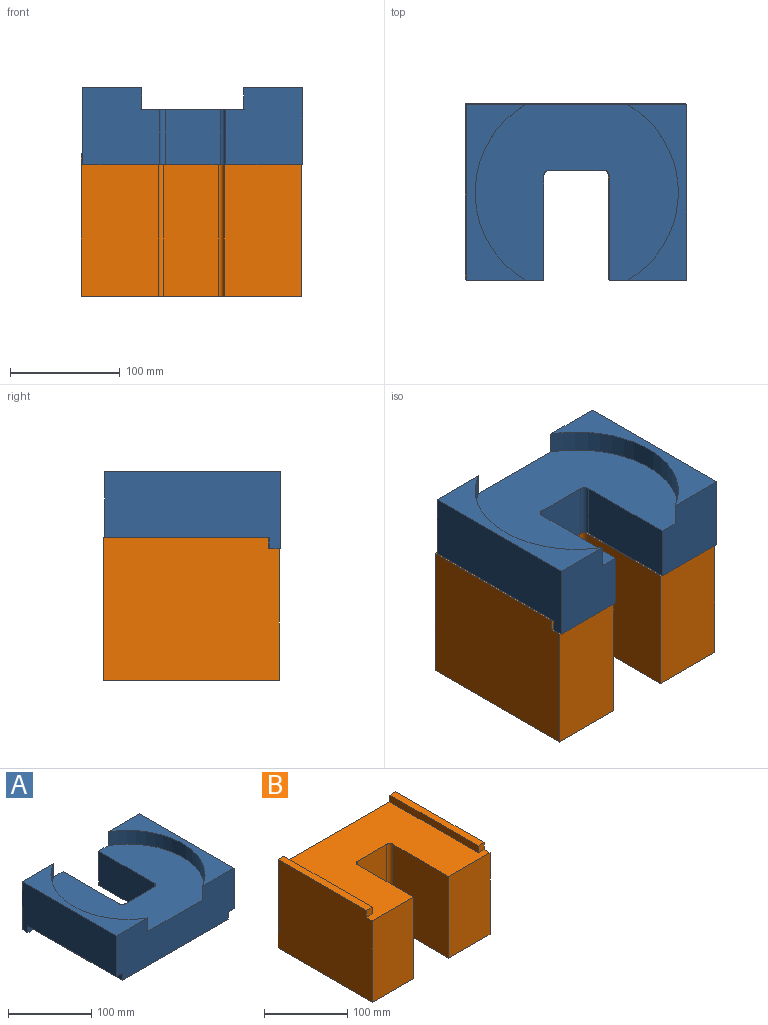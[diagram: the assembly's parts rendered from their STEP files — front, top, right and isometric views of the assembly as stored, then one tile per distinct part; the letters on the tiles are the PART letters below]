
ASSEMBLY  parts=2 mates=1
PART A: 22 faces, bbox 200x160x70 mm
  f0: plane 200x70mm, normal (0,-1,0), area 11942.6mm2, adj f1,f2,f4,f5,f7,f8,f9,f10
  f1: plane 160x70mm, normal (-1,0,0), area 9700mm2, adj f0,f4,f6,f8,f14,f16
  f2: plane 185x160mm, normal (0,0,1), area 19320.9mm2, adj f0,f3,f6,f7,f9,f11,f12,f13
  f3: plane 70x70mm, normal (0,1,0), area 4571.3mm2, adj f2,f4,f5,f9,f10,f12
  f4: plane 200x160mm, normal (0,0,-1), area 23010.7mm2, adj f0,f1,f3,f5,f6,f11,f12,f13
  f5: plane 160x70mm, normal (1,0,0), area 9700mm2, adj f0,f3,f4,f10,f17,f19
  f6: plane 70x70mm, normal (0,1,0), area 4571.3mm2, adj f1,f2,f4,f7,f8,f13
  f7: cylinder r=92.5mm len=160mm, axis (0,0,-1), area 3866.1mm2, adj f0,f2,f6,f8
  f8: plane 160x53.56mm, normal (0,0,1), area 3344.9mm2, adj f0,f1,f6,f7
  f9: cylinder r=92.5mm len=160mm, axis (0,0,-1), area 3866.1mm2, adj f0,f2,f3,f10
  f10: plane 160x53.56mm, normal (0,0,1), area 3344.9mm2, adj f0,f3,f5,f9
  f11: plane 50x50mm, normal (0,1,0), area 2500mm2, adj f2,f4,f20,f21
  f12: plane 95x50mm, normal (-1,0,0), area 4750mm2, adj f2,f3,f4,f21
  f13: plane 95x50mm, normal (1,0,0), area 4750mm2, adj f2,f4,f6,f20
  f14: plane 150x10mm, normal (0,0,-1), area 1500mm2, adj f0,f1,f15,f16
  f15: plane 150x10mm, normal (-1,0,0), area 1500mm2, adj f0,f4,f14,f16
  f16: plane 10x10mm, normal (0,-1,0), area 100mm2, adj f1,f4,f14,f15
  f17: plane 150x10mm, normal (0,0,-1), area 1500mm2, adj f0,f5,f18,f19
  f18: plane 150x10mm, normal (1,0,0), area 1500mm2, adj f0,f4,f17,f19
  f19: plane 10x10mm, normal (0,-1,0), area 100mm2, adj f4,f5,f17,f18
  f20: cylinder r=5mm len=50mm, axis (0,0,1), area 392.7mm2, adj f2,f4,f11,f13
  f21: cylinder r=5mm len=50mm, axis (0,0,-1), area 392.7mm2, adj f2,f4,f11,f12
PART B: 26 faces, bbox 200x160x130 mm
  f0: plane 200x160mm, normal (0,0,1), area 23010.7mm2, adj f1,f2,f3,f4,f5,f6,f7,f8
  f1: plane 120x95mm, normal (-1,0,0), area 11400mm2, adj f0,f2,f9,f25
  f2: plane 120x70mm, normal (0,-1,0), area 8400mm2, adj f0,f1,f3,f9
  f3: plane 160x130mm, normal (1,0,0), area 20700mm2, adj f0,f2,f4,f9,f11,f12
  f4: plane 200x130mm, normal (0,1,0), area 24200mm2, adj f0,f3,f5,f9,f10,f11,f13,f14
  f5: plane 160x130mm, normal (-1,0,0), area 20700mm2, adj f0,f4,f6,f9,f13,f15
  f6: plane 120x70mm, normal (0,-1,0), area 8400mm2, adj f0,f5,f7,f9
  f7: plane 120x95mm, normal (1,0,0), area 11400mm2, adj f0,f6,f9,f24
  f8: plane 120x50mm, normal (0,-1,0), area 6000mm2, adj f0,f9,f24,f25
  f9: plane 200x160mm, normal (0,0,-1), area 25756.3mm2, adj f1,f2,f3,f4,f5,f6,f7,f8
  f10: plane 150x10mm, normal (-1,0,0), area 1500mm2, adj f0,f4,f11,f12
  f11: plane 150x10mm, normal (0,0,1), area 1500mm2, adj f3,f4,f10,f12
  f12: plane 10x10mm, normal (0,-1,0), area 100mm2, adj f0,f3,f10,f11
  f13: plane 150x10mm, normal (0,0,1), area 1500mm2, adj f4,f5,f14,f15
  f14: plane 150x10mm, normal (1,0,0), area 1500mm2, adj f0,f4,f13,f15
  f15: plane 10x10mm, normal (0,-1,0), area 100mm2, adj f0,f5,f13,f14
  f16: cone r=0mm half-angle=59deg, axis (0,0,-1), area 74.2mm2, adj f17
  f17: cylinder r=4.5mm len=15mm, axis (0,0,-1), area 424.1mm2, adj f9,f16
  f18: cone r=0mm half-angle=59deg, axis (0,0,-1), area 74.2mm2, adj f19
  f19: cylinder r=4.5mm len=15mm, axis (0,0,-1), area 424.1mm2, adj f9,f18
  f20: cone r=0mm half-angle=59deg, axis (0,0,-1), area 74.2mm2, adj f21
  f21: cylinder r=4.5mm len=15mm, axis (0,0,-1), area 424.1mm2, adj f9,f20
  f22: cone r=0mm half-angle=59deg, axis (0,0,-1), area 74.2mm2, adj f23
  f23: cylinder r=4.5mm len=15mm, axis (0,0,-1), area 424.1mm2, adj f9,f22
  f24: cylinder r=5mm len=120mm, axis (0,0,1), area 942.5mm2, adj f0,f7,f8,f9
  f25: cylinder r=5mm len=120mm, axis (0,0,-1), area 942.5mm2, adj f0,f1,f8,f9
PLACE A rot(axis=(0,0,-1),180deg) t=(-41.96,-63.13,16.9)mm
PLACE B rot(axis=(0,0,1),0deg) t=(-43.17,-62.15,-103.1)mm
MATE planar B.f0 <-> A.f4  axis (0,0,1) through (-43.17,-54.97,16.9)mm
